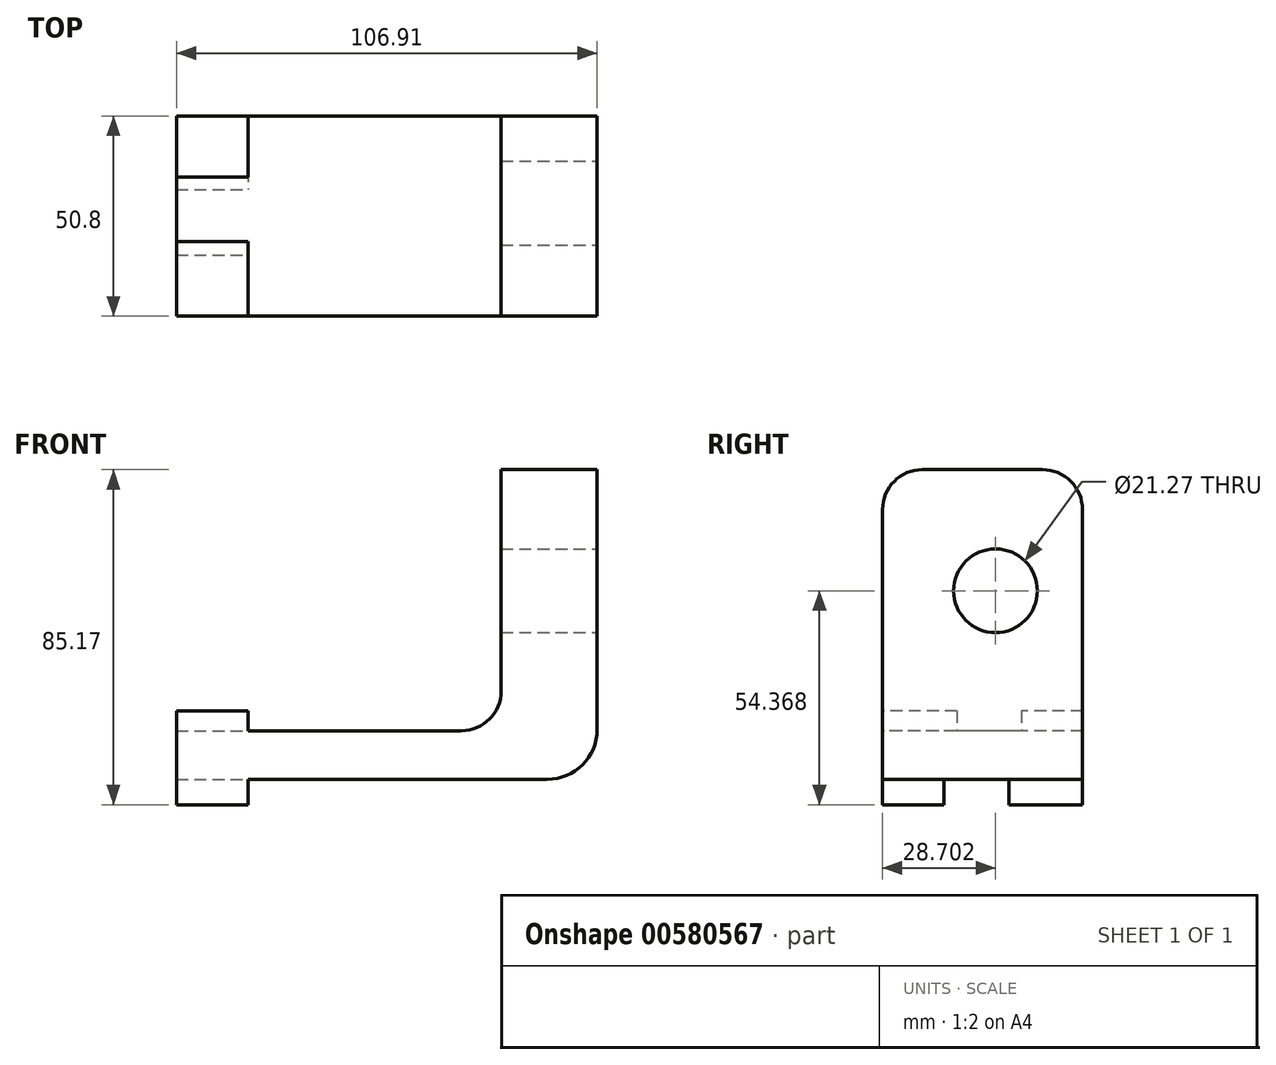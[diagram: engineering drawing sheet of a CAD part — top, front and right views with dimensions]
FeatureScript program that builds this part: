
annotation { "Feature Type Name" : "Feature", "Feature Type Description" : "" }
export const myFeature = defineFeature(function(context is Context, id is Id, definition is map)
    precondition{}
    {
        {
            var Q0;
            Q0=qCreatedBy(makeId("Front.planeOp"),FACE);
            var sketch = newSketch(context, id + "F0", { "sketchPlane" : qUnion([Q0])});
            skLineSegment(sketch, "E0.bottom", {"start": v(4.55, 42.73) * mm, "end": v(28.93, 42.73) * mm});
            skLineSegment(sketch, "E0.top", {"start": v(4.55, -35.98) * mm, "end": v(28.93, -35.98) * mm});
            skLineSegment(sketch, "E0.left", {"start": v(4.55, 42.73) * mm, "end": v(4.55, -23.64) * mm});
            skLineSegment(sketch, "E0.right", {"start": v(28.93, 42.73) * mm, "end": v(28.93, -35.98) * mm});
            skLineSegment(sketch, "E1", {"start": v(4.55, -35.98) * mm, "end": v(-59.77, -35.98) * mm});
            skLineSegment(sketch, "E2", {"start": v(-59.77, -35.98) * mm, "end": v(-59.77, -42.44) * mm});
            skLineSegment(sketch, "E3", {"start": v(-59.77, -42.44) * mm, "end": v(-77.98, -42.44) * mm});
            skLineSegment(sketch, "E4", {"start": v(-77.98, -42.44) * mm, "end": v(-77.98, -18.65) * mm});
            skLineSegment(sketch, "E5", {"start": v(-77.98, -18.65) * mm, "end": v(-59.77, -18.65) * mm});
            skLineSegment(sketch, "E6", {"start": v(-59.77, -18.65) * mm, "end": v(-59.77, -23.64) * mm});
            skLineSegment(sketch, "E7", {"start": v(-59.77, -23.64) * mm, "end": v(4.55, -23.64) * mm});
            skSolve(sketch);
        }
        {
            var Q0;
            Q0=makeQuery(id+"F0.imprint","IMPRINT",FACE,{"disambiguationData":[TD([[makeQuery(id+"F0.imprint","IMPRINT",EDGE,{"derivedFrom":sQuery(id+"F0.wireOp",EDGE,"E0.bottom")}),-1.0]])]});
            extrude(context, id + "F1", {"entities" : qUnion([Q0]), "endBound" : BoundingType.SYMMETRIC, "oppositeDirection" : true, "depth" : 50.8 * mm, "offsetDistance" : 25.4 * mm});
        }
        {
            var Q0;
            Q0=makeQuery(id+"F1.opExtrude","SWEPT_EDGE",EDGE,{"disambiguationData":[OSD([sQuery(id+"F0.wireOp",EDGE,"E0.left"),sQuery(id+"F0.wireOp",EDGE,"E7")])]});
            var Q1;
            Q1=makeQuery(id+"F1.opExtrude","CAP_EDGE",EDGE,{"disambiguationData":[OSD([sQuery(id+"F0.wireOp",EDGE,"E0.bottom")])],"isStart":true});
            var Q2;
            Q2=makeQuery(id+"F1.opExtrude","CAP_EDGE",EDGE,{"disambiguationData":[OSD([sQuery(id+"F0.wireOp",EDGE,"E0.bottom")])],"isStart":false});
            fillet(context, id + "F2", {"entities" : qUnion([Q0, Q1, Q2]), "radius" : 10.16 * mm, "tangentPropagation" : true, "allowEdgeOverflow" : false});
        }
        {
            var Q0;
            Q0=makeQuery(id+"F1.opExtrude","SWEPT_FACE",FACE,{"disambiguationData":[OSD([sQuery(id+"F0.wireOp",EDGE,"E6")])]});
            var sketch = newSketch(context, id + "F3", { "sketchPlane" : qUnion([Q0])});
            skLineSegment(sketch, "E8.bottom", {"start": v(-6.53, -18.65) * mm, "end": v(9.87, -18.65) * mm});
            skLineSegment(sketch, "E8.top", {"start": v(-6.53, -23.64) * mm, "end": v(9.87, -23.64) * mm});
            skLineSegment(sketch, "E8.left", {"start": v(-6.53, -18.65) * mm, "end": v(-6.53, -23.64) * mm});
            skLineSegment(sketch, "E8.right", {"start": v(9.87, -18.65) * mm, "end": v(9.87, -23.64) * mm});
            skSolve(sketch);
        }
        {
            var Q0;
            Q0=makeQuery(id+"F3.imprint","IMPRINT",FACE,{"disambiguationData":[TD([[makeQuery(id+"F3.imprint","IMPRINT",EDGE,{"derivedFrom":sQuery(id+"F3.wireOp",EDGE,"E8.bottom")}),1.0]])]});
            extrude(context, id + "F4", {"entities" : qUnion([Q0]), "operationType" : NewBodyOperationType.REMOVE, "oppositeDirection" : true, "depth" : 50.8 * mm, "offsetDistance" : 25.4 * mm});
        }
        {
            var Q0;
            Q0=makeQuery(id+"F1.opExtrude","SWEPT_FACE",FACE,{"disambiguationData":[OSD([sQuery(id+"F0.wireOp",EDGE,"E2")])]});
            var sketch = newSketch(context, id + "F5", { "sketchPlane" : qUnion([Q0])});
            skLineSegment(sketch, "E9.bottom", {"start": v(-9.83, -42.44) * mm, "end": v(6.75, -42.44) * mm});
            skLineSegment(sketch, "E9.top", {"start": v(-9.83, -35.98) * mm, "end": v(6.75, -35.98) * mm});
            skLineSegment(sketch, "E9.left", {"start": v(-9.83, -42.44) * mm, "end": v(-9.83, -35.98) * mm});
            skLineSegment(sketch, "E9.right", {"start": v(6.75, -42.44) * mm, "end": v(6.75, -35.98) * mm});
            skSolve(sketch);
        }
        {
            var Q0;
            Q0=makeQuery(id+"F5.imprint","IMPRINT",FACE,{"disambiguationData":[TD([[makeQuery(id+"F5.imprint","IMPRINT",EDGE,{"derivedFrom":sQuery(id+"F5.wireOp",EDGE,"E9.bottom")}),-1.0]])]});
            extrude(context, id + "F6", {"entities" : qUnion([Q0]), "operationType" : NewBodyOperationType.REMOVE, "oppositeDirection" : true, "depth" : 50.8 * mm, "offsetDistance" : 25.4 * mm});
        }
        {
            var Q0;
            Q0=makeQuery(id+"F1.opExtrude","SWEPT_FACE",FACE,{"disambiguationData":[OSD([sQuery(id+"F0.wireOp",EDGE,"E0.left")])]});
            var sketch = newSketch(context, id + "F7", { "sketchPlane" : qUnion([Q0])});
            skCircle(sketch, "E10", {"center": v(-3.3, 11.93) * mm, "radius": 10.64 * mm});
            skSolve(sketch);
        }
        {
            var Q0;
            Q0=makeQuery(id+"F7.imprint","IMPRINT",FACE,{"disambiguationData":[TD([[makeQuery(id+"F7.imprint","IMPRINT",EDGE,{"derivedFrom":sQuery(id+"F7.wireOp",EDGE,"E10")}),1.0]])]});
            extrude(context, id + "F8", {"entities" : qUnion([Q0]), "operationType" : NewBodyOperationType.REMOVE, "endBound" : BoundingType.SYMMETRIC, "depth" : 50.8 * mm, "offsetDistance" : 25.4 * mm});
        }
        {
            var Q0;
            Q0=makeQuery(id+"F1.opExtrude","SWEPT_EDGE",EDGE,{"disambiguationData":[OSD([sQuery(id+"F0.wireOp",EDGE,"E0.top"),sQuery(id+"F0.wireOp",EDGE,"E0.right")])]});
            fillet(context, id + "F9", {"entities" : qUnion([Q0]), "radius" : 12.7 * mm, "tangentPropagation" : true, "allowEdgeOverflow" : false});
        }
    });
